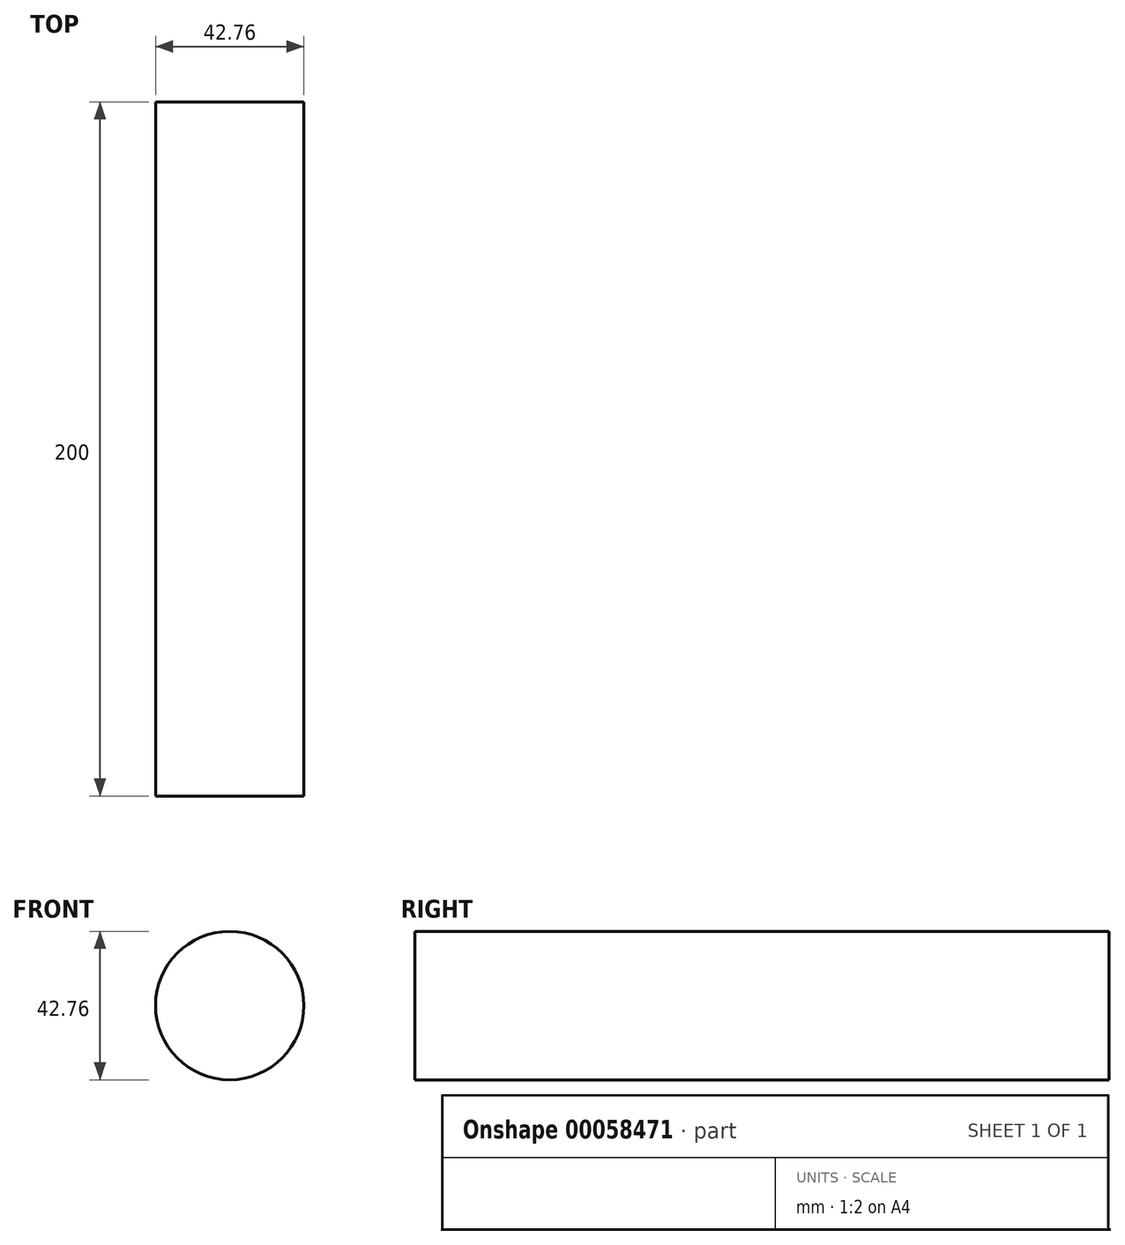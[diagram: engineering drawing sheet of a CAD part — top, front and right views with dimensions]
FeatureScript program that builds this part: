
annotation { "Feature Type Name" : "Feature", "Feature Type Description" : "" }
export const myFeature = defineFeature(function(context is Context, id is Id, definition is map)
    precondition{}
    {
        {
            var Q0;
            Q0=qCreatedBy(makeId("Front.planeOp"),FACE);
            var sketch = newSketch(context, id + "F0", { "sketchPlane" : qUnion([Q0])});
            skCircle(sketch, "E0", {"center": v(0, 0) * mm, "radius": 21.38 * mm});
            skSolve(sketch);
        }
        {
            var Q0;
            Q0=makeQuery(id+"F0.imprint","IMPRINT",FACE,{"disambiguationData":[TD([[makeQuery(id+"F0.imprint","IMPRINT",EDGE,{"derivedFrom":sQuery(id+"F0.wireOp",EDGE,"E0")}),1.0]])]});
            extrude(context, id + "F1", {"entities" : qUnion([Q0]), "depth" : 200 * mm});
        }
    });
